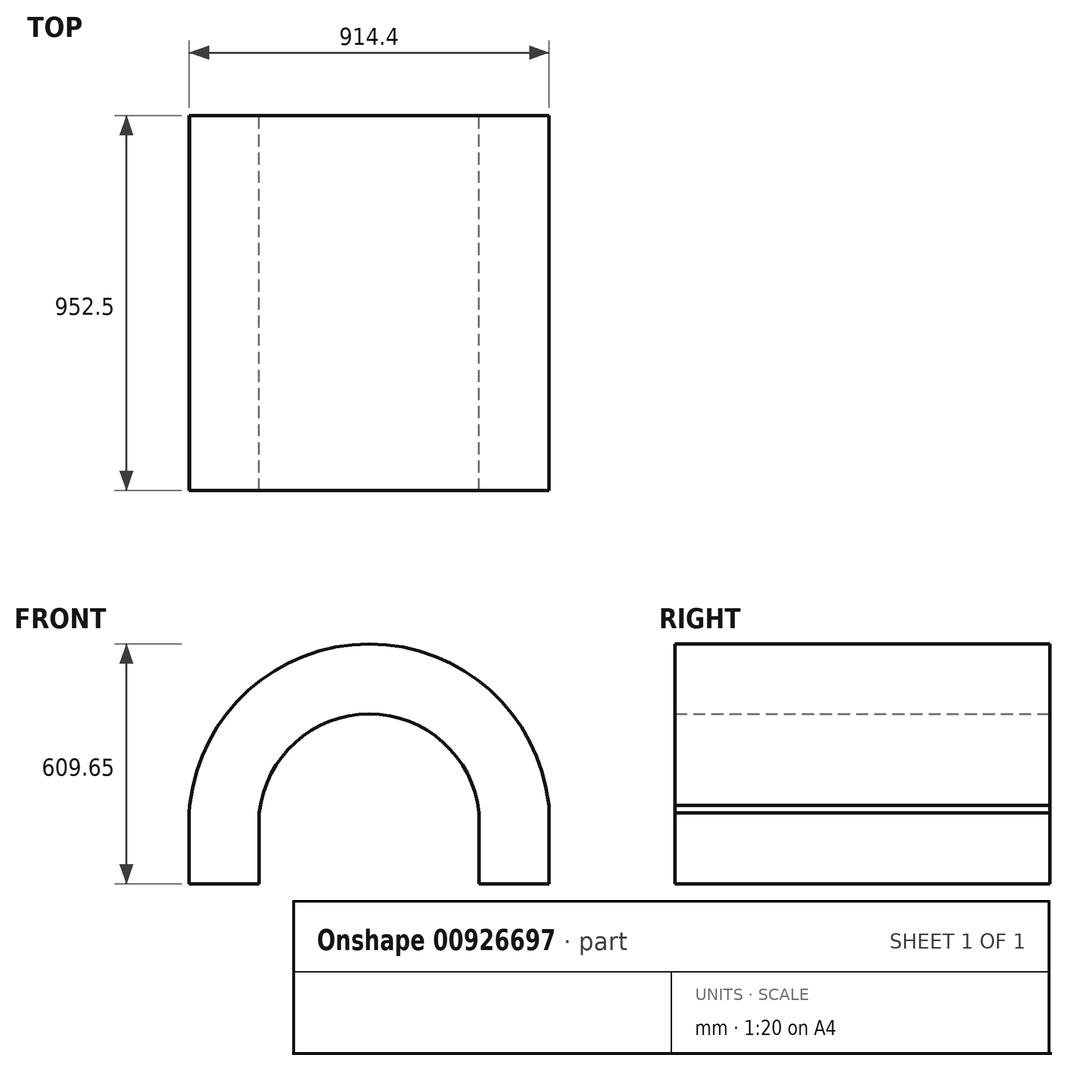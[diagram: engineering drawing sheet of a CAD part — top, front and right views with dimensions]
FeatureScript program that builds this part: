
annotation { "Feature Type Name" : "Feature", "Feature Type Description" : "" }
export const myFeature = defineFeature(function(context is Context, id is Id, definition is map)
    precondition{}
    {
        {
            var Q0;
            Q0=qCreatedBy(makeId("Front.planeOp"),FACE);
            var sketch = newSketch(context, id + "F0", { "sketchPlane" : qUnion([Q0])});
            skLineSegment(sketch, "E0", {"start": v(0, 0) * mm, "end": v(0, 120.65) * mm});
            skLineSegment(sketch, "E1", {"start": v(558.8, 0) * mm, "end": v(558.8, 120.65) * mm});
            skArc(sketch, "E2", {"start": v(558.8, 181) * mm, "mid": v(279.4, 431.85) * mm, "end": v(0, 181) * mm});
            skLineSegment(sketch, "E3", {"start": v(0, 120.65) * mm, "end": v(0, 181) * mm});
            skLineSegment(sketch, "E4", {"start": v(558.8, 120.65) * mm, "end": v(558.8, 181) * mm});
            skLineSegment(sketch, "E5.0", {"start": v(-177.8, 0) * mm, "end": v(-177.8, 120.65) * mm});
            skLineSegment(sketch, "E6.0", {"start": v(-177.8, 120.65) * mm, "end": v(-177.8, 181) * mm});
            skArc(sketch, "E7.0", {"start": v(735.57, 200.1) * mm, "mid": v(279.4, 609.65) * mm, "end": v(-176.77, 200.1) * mm});
            skLineSegment(sketch, "E8.0", {"start": v(736.6, 120.65) * mm, "end": v(736.6, 181) * mm});
            skLineSegment(sketch, "E9.0", {"start": v(736.6, 0) * mm, "end": v(736.6, 120.65) * mm});
            skLineSegment(sketch, "E10", {"start": v(-177.8, 0) * mm, "end": v(0, 0) * mm});
            skLineSegment(sketch, "E11", {"start": v(558.8, 0) * mm, "end": v(736.6, 0) * mm});
            skLineSegment(sketch, "E12", {"start": v(736.6, 181) * mm, "end": v(735.57, 200.1) * mm});
            skLineSegment(sketch, "E13", {"start": v(-177.8, 181) * mm, "end": v(-176.77, 200.1) * mm});
            skSolve(sketch);
        }
        {
            var Q0;
            Q0 = qSketchRegion(id + "F0", true);
            extrude(context, id + "F1", {"entities" : qUnion([Q0]), "depth" : 952.5 * mm, "offsetDistance" : 25.4 * mm});
        }
    });
